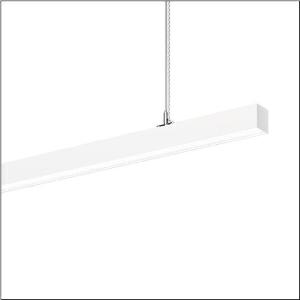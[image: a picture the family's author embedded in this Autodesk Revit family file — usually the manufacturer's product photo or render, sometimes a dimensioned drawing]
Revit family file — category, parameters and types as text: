
# Revit family: silica_r__21_51mx30tat4w_7b2a
name_source: partatom
category: Lighting Fixtures
units: mm (PartAtom-declared; Revit-internal decimal feet)

## family parameters
Cut with Voids When Loaded = No
Host = Face
Light Source = No
Part Type = Normal
Room Calculation Point = No
Round Connector Dimension = Use Diameter
Shared = No

## types (1)
- --- (1 x LED, 4120 lm, 33.8 W, 6500K)
    Apparent Load = 34 VA
    CIE Flux Codes = 47 79 96 58 100
    Color Rendering = 80
    Color Temperature = 6500K
    Default Elevation = 1800 mm
    Description = Silica® 21, office luminaire, primary optical cover: cover, of PMMA, opal, light emission: direct/indirect distribution, primary light characteristic: symmetric, installation type: suspended mounting, LED, rated luminous flux: 4.120lm, luminous efficacy: 116lm/W, light colour: 8tw, colour temperature: 2700..6500K, control gear: ECG DALI, with terminal, 3+2-pole, max. 2.5mm², mains connection: 220..240V, AC, 50/60Hz, rated input power: 35.5W, luminaire housing, of aluminium, traffic white (RAL 9016), length: 1.204mm, width: 53mm, height: 53mm, protection rating (complete): IP20, insulation class (complete): insulation class I (protective earthing), certification: CE, permissible operating ambient temperature: 0..+35°C, standard: EN 50419, packaging unit: 1 piece
    Height = 53 mm
    Lamp = 1 x LED
    Lamp Light Flux = 4120 lm
    Lamp Power = 33.8 W
    Lamp count = 1
    Length = 1204 mm
    Luminous efficacy = 122 lm/W
    Manufacturer = Siteco
    ModVariant = No
    Model = 51MX30TAT4W
    Mounting Place = Ceiling
    Mounting Type = Pendant
    Number of Poles = 1
    OnlyDefault = Yes
    Power Factor = 1
    Product Name = Silica® 21
    Product group = office luminaire | ceiling pendant
    ProductGroupID = 902
    Protection Class = Protection class I
    Protection Degree = IP 20
    RLX_Detail_Level = 1
    RLX_Emergency_Light_Flux = 0 lm
    RLX_Emergency_Type = 0
    RLX_Emergency_Type_DB = No
    RlxData = <blob elided: 18165 chars, md5=da34f7e3>
    Socket = socket
    Standby Power = 0 W
    System Light Flux = 4120 lm
    System Power = 34 W
    Type Comments = individual setting
    Type Image = l_1297784.jpg
    URL = http://relux.com
    VarID = @adj_070981
    Voltage = 0 V
    Weight = 0.00 kg
    Width = 53 mm

## geometry (parser evidence)
native form markers: Blend x4, Sweep x13
no freeform markers — native parametric forms only
